# Revit family: FU_Seat_LAPSE 0230TA
name_source: partatom
category: Furniture
units: mm (PartAtom-declared; Revit-internal decimal feet)

## family parameters
Always vertical = Yes
Cut with Voids When Loaded = No
OmniClass Number = 23.40.20.00
OmniClass Title = General Furniture and Specialties
Render Appearance Source = Family Geometry
Room Calculation Point = No
Shared = No
Work Plane-Based = No

## types (1)
- LAP0230TA
    Default Elevation = 333 mm  [stored 1.09252 ft]
    Depth = 720 mm  [stored 2.3622 ft]
    Description = Upholstered seat with high backrest in the Lapse modular sofa range, 72cm x 72cm / 28.3" x 28.3".
    Height = 553 mm  [stored 1.8143 ft]
    Manufacturer = Sandler
    Model = LAP0230TA
    URL = https://www.sandlerseating.com
    Width = 720 mm  [stored 2.3622 ft]

note: [stored X ft] marks values corroborated as IEEE doubles in the binary element streams (Revit-internal decimal feet)

## geometry (parser evidence)
native form markers: Sweep x3
no freeform markers — native parametric forms only
